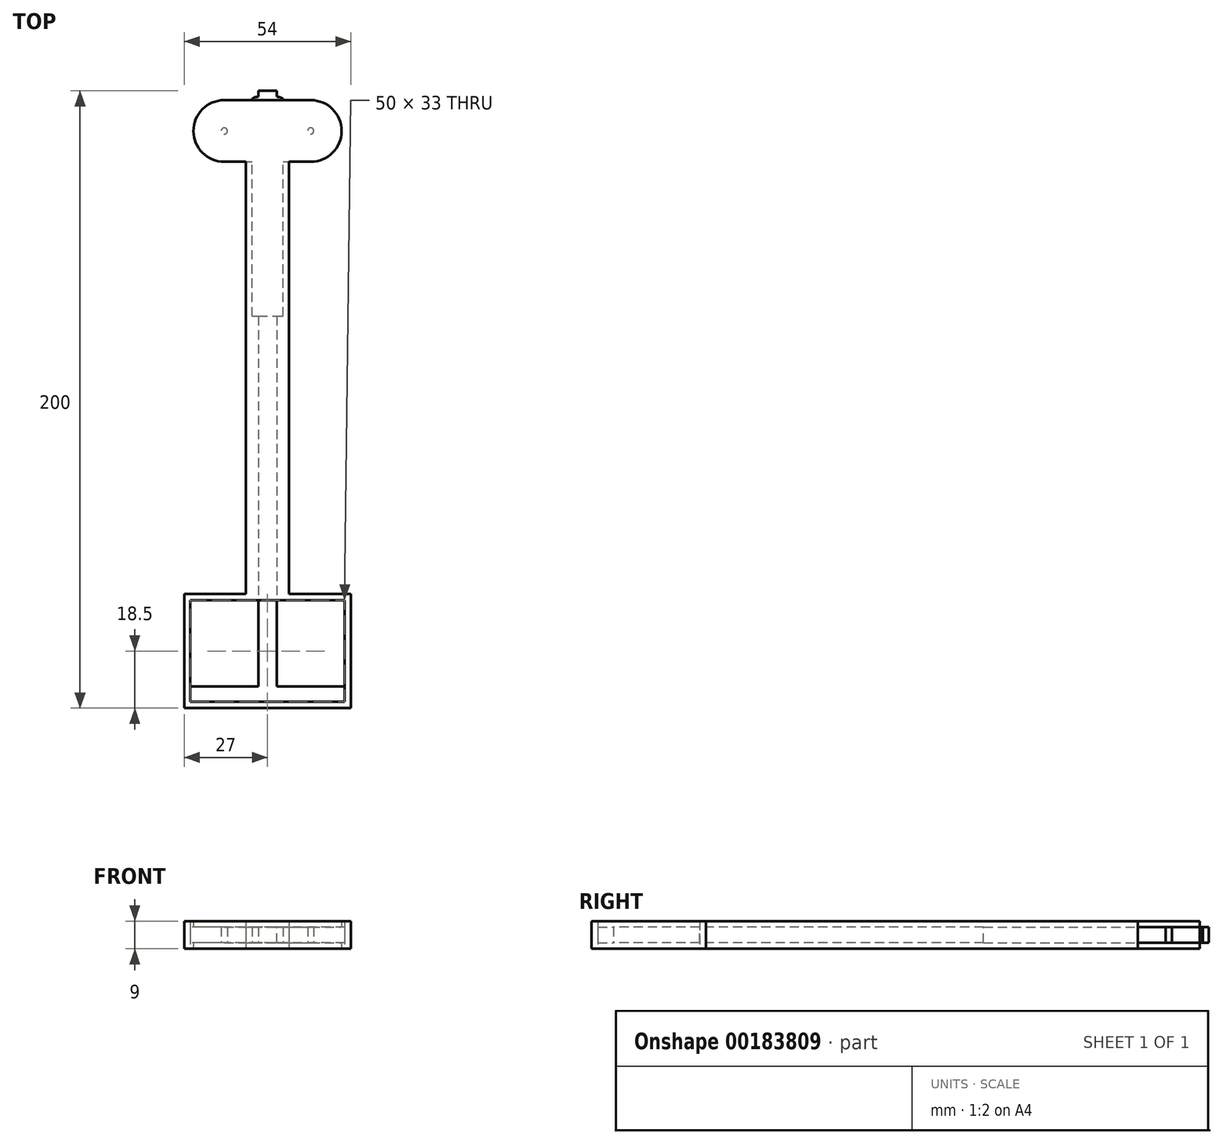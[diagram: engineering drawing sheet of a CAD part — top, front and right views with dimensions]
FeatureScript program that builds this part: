
annotation { "Feature Type Name" : "Feature", "Feature Type Description" : "" }
export const myFeature = defineFeature(function(context is Context, id is Id, definition is map)
    precondition{}
    {
        {
            var Q0;
            Q0=qCreatedBy(makeId("Top.planeOp"),FACE);
            var sketch = newSketch(context, id + "F0", { "sketchPlane" : qUnion([Q0])});
            skLineSegment(sketch, "E0.bottom", {"start": v(0, 13) * mm, "end": v(3, 13) * mm});
            skLineSegment(sketch, "E0.top", {"start": v(0, -180) * mm, "end": v(3, -180) * mm});
            skLineSegment(sketch, "E0.left", {"start": v(0, 13) * mm, "end": v(0, -180) * mm});
            skLineSegment(sketch, "E0.right", {"start": v(3, 13) * mm, "end": v(3, -180) * mm});
            skLineSegment(sketch, "E1", {"start": v(0, 10) * mm, "end": v(3, 10) * mm, "construction": true});
            skArc(sketch, "E2", {"start": v(3, 11.09) * mm, "mid": v(4.04, 10.94) * mm, "end": v(5, 10.5) * mm});
            skLineSegment(sketch, "E3", {"start": v(5, 10.5) * mm, "end": v(5, 10) * mm});
            skArc(sketch, "E4.MirrorCS", {"start": v(3, 8.91) * mm, "mid": v(4.04, 9.06) * mm, "end": v(5, 9.5) * mm});
            skLineSegment(sketch, "E5.MirrorCS", {"start": v(5, 9.5) * mm, "end": v(5, 10) * mm});
            skArc(sketch, "E6.1.0.0", {"start": v(3, 7.89) * mm, "mid": v(4.04, 7.74) * mm, "end": v(5, 7.3) * mm});
            skLineSegment(sketch, "E6.1.0.1", {"start": v(5, 7.3) * mm, "end": v(5, 6.8) * mm});
            skLineSegment(sketch, "E6.1.0.2", {"start": v(5, 6.3) * mm, "end": v(5, 6.8) * mm});
            skArc(sketch, "E6.1.0.3", {"start": v(3, 5.71) * mm, "mid": v(4.04, 5.86) * mm, "end": v(5, 6.3) * mm});
            skArc(sketch, "E6.2.0.0", {"start": v(3, 4.69) * mm, "mid": v(4.04, 4.54) * mm, "end": v(5, 4.1) * mm});
            skLineSegment(sketch, "E6.2.0.1", {"start": v(5, 4.1) * mm, "end": v(5, 3.6) * mm});
            skLineSegment(sketch, "E6.2.0.2", {"start": v(5, 3.1) * mm, "end": v(5, 3.6) * mm});
            skArc(sketch, "E6.2.0.3", {"start": v(3, 2.51) * mm, "mid": v(4.04, 2.66) * mm, "end": v(5, 3.1) * mm});
            skLineSegment(sketch, "E6.direction1", {"start": v(3, 7.39) * mm, "end": v(3, 4.19) * mm, "construction": true});
            skArc(sketch, "E7.0.3.0", {"start": v(3, 1.49) * mm, "mid": v(4.04, 1.34) * mm, "end": v(5, 0.9) * mm});
            skLineSegment(sketch, "E7.4.3.0", {"start": v(5, 0.9) * mm, "end": v(5, 0.4) * mm});
            skLineSegment(sketch, "E7.7.3.0", {"start": v(5, -0.1) * mm, "end": v(5, 0.4) * mm});
            skArc(sketch, "E7.10.3.0", {"start": v(3, -0.69) * mm, "mid": v(4.04, -0.54) * mm, "end": v(5, -0.1) * mm});
            skArc(sketch, "E7.0.4.0", {"start": v(3, -1.71) * mm, "mid": v(4.04, -1.86) * mm, "end": v(5, -2.3) * mm});
            skLineSegment(sketch, "E7.4.4.0", {"start": v(5, -2.3) * mm, "end": v(5, -2.8) * mm});
            skLineSegment(sketch, "E7.7.4.0", {"start": v(5, -3.3) * mm, "end": v(5, -2.8) * mm});
            skArc(sketch, "E7.10.4.0", {"start": v(3, -3.89) * mm, "mid": v(4.04, -3.74) * mm, "end": v(5, -3.3) * mm});
            skArc(sketch, "E7.0.5.0", {"start": v(3, -4.91) * mm, "mid": v(4.04, -5.06) * mm, "end": v(5, -5.5) * mm});
            skLineSegment(sketch, "E7.4.5.0", {"start": v(5, -5.5) * mm, "end": v(5, -6) * mm});
            skLineSegment(sketch, "E7.7.5.0", {"start": v(5, -6.5) * mm, "end": v(5, -6) * mm});
            skArc(sketch, "E7.10.5.0", {"start": v(3, -7.09) * mm, "mid": v(4.04, -6.94) * mm, "end": v(5, -6.5) * mm});
            skArc(sketch, "E7.0.6.0", {"start": v(3, -8.11) * mm, "mid": v(4.04, -8.26) * mm, "end": v(5, -8.7) * mm});
            skLineSegment(sketch, "E7.4.6.0", {"start": v(5, -8.7) * mm, "end": v(5, -9.2) * mm});
            skLineSegment(sketch, "E7.7.6.0", {"start": v(5, -9.7) * mm, "end": v(5, -9.2) * mm});
            skArc(sketch, "E7.10.6.0", {"start": v(3, -10.29) * mm, "mid": v(4.04, -10.14) * mm, "end": v(5, -9.7) * mm});
            skArc(sketch, "E7.0.7.0", {"start": v(3, -11.31) * mm, "mid": v(4.04, -11.46) * mm, "end": v(5, -11.9) * mm});
            skLineSegment(sketch, "E7.4.7.0", {"start": v(5, -11.9) * mm, "end": v(5, -12.4) * mm});
            skLineSegment(sketch, "E7.7.7.0", {"start": v(5, -12.9) * mm, "end": v(5, -12.4) * mm});
            skArc(sketch, "E7.10.7.0", {"start": v(3, -13.49) * mm, "mid": v(4.04, -13.34) * mm, "end": v(5, -12.9) * mm});
            skArc(sketch, "E7.0.8.0", {"start": v(3, -14.51) * mm, "mid": v(4.04, -14.66) * mm, "end": v(5, -15.1) * mm});
            skLineSegment(sketch, "E7.4.8.0", {"start": v(5, -15.1) * mm, "end": v(5, -15.6) * mm});
            skLineSegment(sketch, "E7.7.8.0", {"start": v(5, -16.1) * mm, "end": v(5, -15.6) * mm});
            skArc(sketch, "E7.10.8.0", {"start": v(3, -16.69) * mm, "mid": v(4.04, -16.54) * mm, "end": v(5, -16.1) * mm});
            skArc(sketch, "E7.0.9.0", {"start": v(3, -17.71) * mm, "mid": v(4.04, -17.86) * mm, "end": v(5, -18.3) * mm});
            skLineSegment(sketch, "E7.4.9.0", {"start": v(5, -18.3) * mm, "end": v(5, -18.8) * mm});
            skLineSegment(sketch, "E7.7.9.0", {"start": v(5, -19.3) * mm, "end": v(5, -18.8) * mm});
            skArc(sketch, "E7.10.9.0", {"start": v(3, -19.89) * mm, "mid": v(4.04, -19.74) * mm, "end": v(5, -19.3) * mm});
            skArc(sketch, "E7.0.10.0", {"start": v(3, -20.91) * mm, "mid": v(4.04, -21.06) * mm, "end": v(5, -21.5) * mm});
            skLineSegment(sketch, "E7.4.10.0", {"start": v(5, -21.5) * mm, "end": v(5, -22) * mm});
            skLineSegment(sketch, "E7.7.10.0", {"start": v(5, -22.5) * mm, "end": v(5, -22) * mm});
            skArc(sketch, "E7.10.10.0", {"start": v(3, -23.09) * mm, "mid": v(4.04, -22.94) * mm, "end": v(5, -22.5) * mm});
            skArc(sketch, "E7.0.11.0", {"start": v(3, -24.11) * mm, "mid": v(4.04, -24.26) * mm, "end": v(5, -24.7) * mm});
            skLineSegment(sketch, "E7.4.11.0", {"start": v(5, -24.7) * mm, "end": v(5, -25.2) * mm});
            skLineSegment(sketch, "E7.7.11.0", {"start": v(5, -25.7) * mm, "end": v(5, -25.2) * mm});
            skArc(sketch, "E7.10.11.0", {"start": v(3, -26.29) * mm, "mid": v(4.04, -26.14) * mm, "end": v(5, -25.7) * mm});
            skArc(sketch, "E7.0.12.0", {"start": v(3, -27.31) * mm, "mid": v(4.04, -27.46) * mm, "end": v(5, -27.9) * mm});
            skLineSegment(sketch, "E7.4.12.0", {"start": v(5, -27.9) * mm, "end": v(5, -28.4) * mm});
            skLineSegment(sketch, "E7.7.12.0", {"start": v(5, -28.9) * mm, "end": v(5, -28.4) * mm});
            skArc(sketch, "E7.10.12.0", {"start": v(3, -29.49) * mm, "mid": v(4.04, -29.34) * mm, "end": v(5, -28.9) * mm});
            skArc(sketch, "E7.0.13.0", {"start": v(3, -30.51) * mm, "mid": v(4.04, -30.66) * mm, "end": v(5, -31.1) * mm});
            skLineSegment(sketch, "E7.4.13.0", {"start": v(5, -31.1) * mm, "end": v(5, -31.6) * mm});
            skLineSegment(sketch, "E7.7.13.0", {"start": v(5, -32.1) * mm, "end": v(5, -31.6) * mm});
            skArc(sketch, "E7.10.13.0", {"start": v(3, -32.69) * mm, "mid": v(4.04, -32.54) * mm, "end": v(5, -32.1) * mm});
            skArc(sketch, "E7.0.14.0", {"start": v(3, -33.71) * mm, "mid": v(4.04, -33.86) * mm, "end": v(5, -34.3) * mm});
            skLineSegment(sketch, "E7.4.14.0", {"start": v(5, -34.3) * mm, "end": v(5, -34.8) * mm});
            skLineSegment(sketch, "E7.7.14.0", {"start": v(5, -35.3) * mm, "end": v(5, -34.8) * mm});
            skArc(sketch, "E7.10.14.0", {"start": v(3, -35.89) * mm, "mid": v(4.04, -35.74) * mm, "end": v(5, -35.3) * mm});
            skArc(sketch, "E7.0.15.0", {"start": v(3, -36.91) * mm, "mid": v(4.04, -37.06) * mm, "end": v(5, -37.5) * mm});
            skLineSegment(sketch, "E7.4.15.0", {"start": v(5, -37.5) * mm, "end": v(5, -38) * mm});
            skLineSegment(sketch, "E7.7.15.0", {"start": v(5, -38.5) * mm, "end": v(5, -38) * mm});
            skArc(sketch, "E7.10.15.0", {"start": v(3, -39.09) * mm, "mid": v(4.04, -38.94) * mm, "end": v(5, -38.5) * mm});
            skSolve(sketch);
        }
        {
            var Q0;
            Q0 = qSketchRegion(id + "F0", true);
            extrude(context, id + "F1", {"entities" : qUnion([Q0]), "depth" : 5 * mm});
        }
        {
            var Q0;
            Q0=makeQuery(id+"F1.opExtrude","SWEPT_BODY",BODY,{"disambiguationData":[OSD([sQuery(id+"F0.wireOp",EDGE,"E0.bottom"),sQuery(id+"F0.wireOp",EDGE,"E0.top"),sQuery(id+"F0.wireOp",EDGE,"E0.left"),sQuery(id+"F0.wireOp",EDGE,"E0.right"),sQuery(id+"F0.wireOp",EDGE,"E2"),sQuery(id+"F0.wireOp",EDGE,"E3"),sQuery(id+"F0.wireOp",EDGE,"E4.MirrorCS"),sQuery(id+"F0.wireOp",EDGE,"E5.MirrorCS"),sQuery(id+"F0.wireOp",EDGE,"E6.1.0.0"),sQuery(id+"F0.wireOp",EDGE,"E6.1.0.1"),sQuery(id+"F0.wireOp",EDGE,"E6.1.0.2"),sQuery(id+"F0.wireOp",EDGE,"E6.1.0.3"),sQuery(id+"F0.wireOp",EDGE,"E6.2.0.0"),sQuery(id+"F0.wireOp",EDGE,"E6.2.0.1"),sQuery(id+"F0.wireOp",EDGE,"E6.2.0.2"),sQuery(id+"F0.wireOp",EDGE,"E6.2.0.3"),sQuery(id+"F0.wireOp",EDGE,"E7.0.3.0"),sQuery(id+"F0.wireOp",EDGE,"E7.4.3.0"),sQuery(id+"F0.wireOp",EDGE,"E7.7.3.0"),sQuery(id+"F0.wireOp",EDGE,"E7.10.3.0"),sQuery(id+"F0.wireOp",EDGE,"E7.0.4.0"),sQuery(id+"F0.wireOp",EDGE,"E7.4.4.0"),sQuery(id+"F0.wireOp",EDGE,"E7.7.4.0"),sQuery(id+"F0.wireOp",EDGE,"E7.10.4.0"),sQuery(id+"F0.wireOp",EDGE,"E7.0.5.0"),sQuery(id+"F0.wireOp",EDGE,"E7.4.5.0"),sQuery(id+"F0.wireOp",EDGE,"E7.7.5.0"),sQuery(id+"F0.wireOp",EDGE,"E7.10.5.0"),sQuery(id+"F0.wireOp",EDGE,"E7.0.6.0"),sQuery(id+"F0.wireOp",EDGE,"E7.4.6.0"),sQuery(id+"F0.wireOp",EDGE,"E7.7.6.0"),sQuery(id+"F0.wireOp",EDGE,"E7.10.6.0"),sQuery(id+"F0.wireOp",EDGE,"E7.0.7.0"),sQuery(id+"F0.wireOp",EDGE,"E7.4.7.0"),sQuery(id+"F0.wireOp",EDGE,"E7.7.7.0"),sQuery(id+"F0.wireOp",EDGE,"E7.10.7.0"),sQuery(id+"F0.wireOp",EDGE,"E7.0.8.0"),sQuery(id+"F0.wireOp",EDGE,"E7.4.8.0"),sQuery(id+"F0.wireOp",EDGE,"E7.7.8.0"),sQuery(id+"F0.wireOp",EDGE,"E7.10.8.0"),sQuery(id+"F0.wireOp",EDGE,"E7.0.9.0"),sQuery(id+"F0.wireOp",EDGE,"E7.4.9.0"),sQuery(id+"F0.wireOp",EDGE,"E7.7.9.0"),sQuery(id+"F0.wireOp",EDGE,"E7.10.9.0"),sQuery(id+"F0.wireOp",EDGE,"E7.0.10.0"),sQuery(id+"F0.wireOp",EDGE,"E7.4.10.0"),sQuery(id+"F0.wireOp",EDGE,"E7.7.10.0"),sQuery(id+"F0.wireOp",EDGE,"E7.10.10.0"),sQuery(id+"F0.wireOp",EDGE,"E7.0.11.0"),sQuery(id+"F0.wireOp",EDGE,"E7.4.11.0"),sQuery(id+"F0.wireOp",EDGE,"E7.7.11.0"),sQuery(id+"F0.wireOp",EDGE,"E7.10.11.0"),sQuery(id+"F0.wireOp",EDGE,"E7.0.12.0"),sQuery(id+"F0.wireOp",EDGE,"E7.4.12.0"),sQuery(id+"F0.wireOp",EDGE,"E7.7.12.0"),sQuery(id+"F0.wireOp",EDGE,"E7.10.12.0"),sQuery(id+"F0.wireOp",EDGE,"E7.0.13.0"),sQuery(id+"F0.wireOp",EDGE,"E7.4.13.0"),sQuery(id+"F0.wireOp",EDGE,"E7.7.13.0"),sQuery(id+"F0.wireOp",EDGE,"E7.10.13.0"),sQuery(id+"F0.wireOp",EDGE,"E7.0.14.0"),sQuery(id+"F0.wireOp",EDGE,"E7.4.14.0"),sQuery(id+"F0.wireOp",EDGE,"E7.7.14.0"),sQuery(id+"F0.wireOp",EDGE,"E7.10.14.0"),sQuery(id+"F0.wireOp",EDGE,"E7.0.15.0"),sQuery(id+"F0.wireOp",EDGE,"E7.4.15.0"),sQuery(id+"F0.wireOp",EDGE,"E7.7.15.0"),sQuery(id+"F0.wireOp",EDGE,"E7.10.15.0")])]});
            var Q1;
            Q1=makeQuery(id+"F1.opExtrude","SWEPT_FACE",FACE,{"disambiguationData":[OSD([sQuery(id+"F0.wireOp",EDGE,"E0.left")])]});
            mirror(context, id + "F2", {"operationType" : NewBodyOperationType.ADD, "entities" : qUnion([Q0]), "mirrorPlane" : qUnion([Q1])});
        }
        {
            var Q0;
            {var subQ0=makeQuery(id+"F1.opExtrude","SWEPT_FACE",FACE,{"disambiguationData":[OSD([sQuery(id+"F0.wireOp",EDGE,"E0.top")])]});Q0=makeQuery(id+"F2.boolean.opBoolean","MERGE",FACE,{"derivedFrom":[subQ0,makeQuery(id+"F2.opPattern","COPY",FACE,{"derivedFrom":subQ0,"instanceName":"1"})]});}
            var sketch = newSketch(context, id + "F3", { "sketchPlane" : qUnion([Q0])});
            skLineSegment(sketch, "E8.bottom", {"start": v(25, 5) * mm, "end": v(-25, 5) * mm});
            skLineSegment(sketch, "E8.top", {"start": v(25, 0) * mm, "end": v(-25, 0) * mm});
            skLineSegment(sketch, "E8.left", {"start": v(25, 5) * mm, "end": v(25, 0) * mm});
            skLineSegment(sketch, "E8.right", {"start": v(-25, 5) * mm, "end": v(-25, 0) * mm});
            skPoint(sketch, "E8.middle", {"position": v(0, 2.5) * mm});
            skPoint(sketch, "E8.middle.positionSnap0", {"position": v(-3, 2.5) * mm});
            skPoint(sketch, "E8.centerSnap0", {"position": v(-3, 2.5) * mm});
            skSolve(sketch);
        }
        {
            var Q0;
            Q0 = qSketchRegion(id + "F3", true);
            extrude(context, id + "F4", {"entities" : qUnion([Q0]), "operationType" : NewBodyOperationType.ADD, "depth" : 5 * mm});
        }
        {
            var Q0;
            Q0=qCreatedBy(makeId("Top.planeOp"),FACE);
            var sketch = newSketch(context, id + "F5", { "sketchPlane" : qUnion([Q0])});
            skCircle(sketch, "E9", {"center": v(14, 0) * mm, "radius": 10 * mm});
            skLineSegment(sketch, "E10", {"start": v(0, 10) * mm, "end": v(14, 10) * mm});
            skLineSegment(sketch, "E11", {"start": v(0, -187) * mm, "end": v(27, -187) * mm});
            skLineSegment(sketch, "E12", {"start": v(27, -187) * mm, "end": v(27, -150) * mm});
            skLineSegment(sketch, "E13", {"start": v(27, -150) * mm, "end": v(7, -150) * mm});
            skLineSegment(sketch, "E14", {"start": v(7, -150) * mm, "end": v(7, -10) * mm});
            skLineSegment(sketch, "E15", {"start": v(7, -10) * mm, "end": v(14, -10) * mm});
            skLineSegment(sketch, "E16.MirrorCS", {"start": v(0, 10) * mm, "end": v(-14, 10) * mm});
            skCircle(sketch, "E17.MirrorC", {"center": v(-14, 0) * mm, "radius": 10 * mm});
            skLineSegment(sketch, "E18.MirrorCS", {"start": v(-7, -10) * mm, "end": v(-14, -10) * mm});
            skLineSegment(sketch, "E19.MirrorCS", {"start": v(-7, -150) * mm, "end": v(-7, -10) * mm});
            skLineSegment(sketch, "E20.MirrorCS", {"start": v(-27, -150) * mm, "end": v(-7, -150) * mm});
            skLineSegment(sketch, "E21.MirrorCS", {"start": v(-27, -187) * mm, "end": v(-27, -150) * mm});
            skLineSegment(sketch, "E22.MirrorCS", {"start": v(0, -187) * mm, "end": v(-27, -187) * mm});
            skLineSegment(sketch, "E23.bottom", {"start": v(25, -152) * mm, "end": v(-25, -152) * mm});
            skLineSegment(sketch, "E23.top", {"start": v(25, -185) * mm, "end": v(-25, -185) * mm});
            skLineSegment(sketch, "E23.left", {"start": v(25, -152) * mm, "end": v(25, -185) * mm});
            skLineSegment(sketch, "E23.right", {"start": v(-25, -152) * mm, "end": v(-25, -185) * mm});
            skPoint(sketch, "E23.middle", {"position": v(0, -168.5) * mm});
            skSolve(sketch);
        }
        {
            var Q0;
            Q0 = qSketchRegion(id + "F5", true);
            extrude(context, id + "F6", {"entities" : qUnion([Q0]), "depth" : 7 * mm, "hasSecondDirection" : true, "secondDirectionOppositeDirection" : true, "secondDirectionDepth" : 2 * mm});
        }
        {
            var Q0;
            Q0=makeQuery(id+"F1.opExtrude","SWEPT_BODY",BODY,{"disambiguationData":[OSD([sQuery(id+"F0.wireOp",EDGE,"E0.bottom"),sQuery(id+"F0.wireOp",EDGE,"E0.top"),sQuery(id+"F0.wireOp",EDGE,"E0.left"),sQuery(id+"F0.wireOp",EDGE,"E0.right"),sQuery(id+"F0.wireOp",EDGE,"E2"),sQuery(id+"F0.wireOp",EDGE,"E3"),sQuery(id+"F0.wireOp",EDGE,"E4.MirrorCS"),sQuery(id+"F0.wireOp",EDGE,"E5.MirrorCS"),sQuery(id+"F0.wireOp",EDGE,"E6.1.0.0"),sQuery(id+"F0.wireOp",EDGE,"E6.1.0.1"),sQuery(id+"F0.wireOp",EDGE,"E6.1.0.2"),sQuery(id+"F0.wireOp",EDGE,"E6.1.0.3"),sQuery(id+"F0.wireOp",EDGE,"E6.2.0.0"),sQuery(id+"F0.wireOp",EDGE,"E6.2.0.1"),sQuery(id+"F0.wireOp",EDGE,"E6.2.0.2"),sQuery(id+"F0.wireOp",EDGE,"E6.2.0.3"),sQuery(id+"F0.wireOp",EDGE,"E7.0.3.0"),sQuery(id+"F0.wireOp",EDGE,"E7.4.3.0"),sQuery(id+"F0.wireOp",EDGE,"E7.7.3.0"),sQuery(id+"F0.wireOp",EDGE,"E7.10.3.0"),sQuery(id+"F0.wireOp",EDGE,"E7.0.4.0"),sQuery(id+"F0.wireOp",EDGE,"E7.4.4.0"),sQuery(id+"F0.wireOp",EDGE,"E7.7.4.0"),sQuery(id+"F0.wireOp",EDGE,"E7.10.4.0"),sQuery(id+"F0.wireOp",EDGE,"E7.0.5.0"),sQuery(id+"F0.wireOp",EDGE,"E7.4.5.0"),sQuery(id+"F0.wireOp",EDGE,"E7.7.5.0"),sQuery(id+"F0.wireOp",EDGE,"E7.10.5.0"),sQuery(id+"F0.wireOp",EDGE,"E7.0.6.0"),sQuery(id+"F0.wireOp",EDGE,"E7.4.6.0"),sQuery(id+"F0.wireOp",EDGE,"E7.7.6.0"),sQuery(id+"F0.wireOp",EDGE,"E7.10.6.0"),sQuery(id+"F0.wireOp",EDGE,"E7.0.7.0"),sQuery(id+"F0.wireOp",EDGE,"E7.4.7.0"),sQuery(id+"F0.wireOp",EDGE,"E7.7.7.0"),sQuery(id+"F0.wireOp",EDGE,"E7.10.7.0"),sQuery(id+"F0.wireOp",EDGE,"E7.0.8.0"),sQuery(id+"F0.wireOp",EDGE,"E7.4.8.0"),sQuery(id+"F0.wireOp",EDGE,"E7.7.8.0"),sQuery(id+"F0.wireOp",EDGE,"E7.10.8.0"),sQuery(id+"F0.wireOp",EDGE,"E7.0.9.0"),sQuery(id+"F0.wireOp",EDGE,"E7.4.9.0"),sQuery(id+"F0.wireOp",EDGE,"E7.7.9.0"),sQuery(id+"F0.wireOp",EDGE,"E7.10.9.0"),sQuery(id+"F0.wireOp",EDGE,"E7.0.10.0"),sQuery(id+"F0.wireOp",EDGE,"E7.4.10.0"),sQuery(id+"F0.wireOp",EDGE,"E7.7.10.0"),sQuery(id+"F0.wireOp",EDGE,"E7.10.10.0"),sQuery(id+"F0.wireOp",EDGE,"E7.0.11.0"),sQuery(id+"F0.wireOp",EDGE,"E7.4.11.0"),sQuery(id+"F0.wireOp",EDGE,"E7.7.11.0"),sQuery(id+"F0.wireOp",EDGE,"E7.10.11.0"),sQuery(id+"F0.wireOp",EDGE,"E7.0.12.0"),sQuery(id+"F0.wireOp",EDGE,"E7.4.12.0"),sQuery(id+"F0.wireOp",EDGE,"E7.7.12.0"),sQuery(id+"F0.wireOp",EDGE,"E7.10.12.0"),sQuery(id+"F0.wireOp",EDGE,"E7.0.13.0"),sQuery(id+"F0.wireOp",EDGE,"E7.4.13.0"),sQuery(id+"F0.wireOp",EDGE,"E7.7.13.0"),sQuery(id+"F0.wireOp",EDGE,"E7.10.13.0"),sQuery(id+"F0.wireOp",EDGE,"E7.0.14.0"),sQuery(id+"F0.wireOp",EDGE,"E7.4.14.0"),sQuery(id+"F0.wireOp",EDGE,"E7.7.14.0"),sQuery(id+"F0.wireOp",EDGE,"E7.10.14.0"),sQuery(id+"F0.wireOp",EDGE,"E7.0.15.0"),sQuery(id+"F0.wireOp",EDGE,"E7.4.15.0"),sQuery(id+"F0.wireOp",EDGE,"E7.7.15.0"),sQuery(id+"F0.wireOp",EDGE,"E7.10.15.0")])]});
            var Q1;
            Q1=makeQuery(id+"F6.opExtrude","SWEPT_BODY",BODY,{"disambiguationData":[OSD([sQuery(id+"F5.wireOp",EDGE,"E9"),sQuery(id+"F5.wireOp",EDGE,"E10"),sQuery(id+"F5.wireOp",EDGE,"E11"),sQuery(id+"F5.wireOp",EDGE,"E12"),sQuery(id+"F5.wireOp",EDGE,"E13"),sQuery(id+"F5.wireOp",EDGE,"E14"),sQuery(id+"F5.wireOp",EDGE,"E15"),sQuery(id+"F5.wireOp",EDGE,"E16.MirrorCS"),sQuery(id+"F5.wireOp",EDGE,"E17.MirrorC"),sQuery(id+"F5.wireOp",EDGE,"E18.MirrorCS"),sQuery(id+"F5.wireOp",EDGE,"E19.MirrorCS"),sQuery(id+"F5.wireOp",EDGE,"E20.MirrorCS"),sQuery(id+"F5.wireOp",EDGE,"E21.MirrorCS"),sQuery(id+"F5.wireOp",EDGE,"E22.MirrorCS"),sQuery(id+"F5.wireOp",EDGE,"E23.bottom"),sQuery(id+"F5.wireOp",EDGE,"E23.top"),sQuery(id+"F5.wireOp",EDGE,"E23.left"),sQuery(id+"F5.wireOp",EDGE,"E23.right")])]});
            booleanBodies(context, id + "F7", {"operationType" : BooleanOperationType.SUBTRACTION, "tools" : qUnion([Q0]), "targets" : qUnion([Q1]), "keepTools" : true});
        }
        {
            var Q0;
            Q0=qCreatedBy(makeId("Top.planeOp"),FACE);
            var sketch = newSketch(context, id + "F8", { "sketchPlane" : qUnion([Q0])});
            skArc(sketch, "E24.0", {"start": v(-14, -10) * mm, "mid": v(-24, 0) * mm, "end": v(-14, 10) * mm});
            skLineSegment(sketch, "E25.0", {"start": v(-14, 10) * mm, "end": v(14, 10) * mm});
            skArc(sketch, "E26.0", {"start": v(14, -10) * mm, "mid": v(24, 0) * mm, "end": v(14, 10) * mm});
            skLineSegment(sketch, "E27", {"start": v(-14, -10) * mm, "end": v(14, -10) * mm});
            skSolve(sketch);
        }
        {
            var Q0;
            Q0 = qSketchRegion(id + "F8", true);
            extrude(context, id + "F9", {"entities" : qUnion([Q0]), "operationType" : NewBodyOperationType.REMOVE, "depth" : 5 * mm});
        }
        {
            var Q0;
            {var subQ69=sQuery(id+"F8.wireOp",EDGE,"E27");Q0=makeQuery(id+"F9.boolean.opBoolean","COPY",FACE,{"disambiguationData":[TD([makeQuery(id+"F6.opExtrude","SWEPT_FACE",FACE,{"disambiguationData":[OSD([sQuery(id+"F5.wireOp",EDGE,"E18.MirrorCS")])]})])],"derivedFrom":makeQuery(id+"F9.opExtrude","SWEPT_FACE",FACE,{"disambiguationData":[OSD([subQ69])]})});}
            var sketch = newSketch(context, id + "F10", { "sketchPlane" : qUnion([Q0])});
            skLineSegment(sketch, "E28.bottom", {"start": v(5, 5) * mm, "end": v(-5, 5) * mm});
            skLineSegment(sketch, "E28.top", {"start": v(5, 0) * mm, "end": v(-5, 0) * mm});
            skLineSegment(sketch, "E28.left", {"start": v(5, 5) * mm, "end": v(5, 0) * mm});
            skLineSegment(sketch, "E28.right", {"start": v(-5, 5) * mm, "end": v(-5, 0) * mm});
            skSolve(sketch);
        }
        {
            var Q0;
            Q0 = qSketchRegion(id + "F10", true);
            extrude(context, id + "F11", {"entities" : qUnion([Q0]), "operationType" : NewBodyOperationType.REMOVE, "oppositeDirection" : true, "depth" : 50 * mm});
        }
        {
            var Q0;
            Q0=qCreatedBy(makeId("Top.planeOp"),FACE);
            var sketch = newSketch(context, id + "F12", { "sketchPlane" : qUnion([Q0])});
            skCircle(sketch, "E29", {"center": v(14, 0) * mm, "radius": 1 * mm});
            skCircle(sketch, "E30", {"center": v(-14, 0) * mm, "radius": 1 * mm});
            skSolve(sketch);
        }
        {
            var Q0;
            Q0 = qSketchRegion(id + "F12", true);
            extrude(context, id + "F13", {"entities" : qUnion([Q0]), "operationType" : NewBodyOperationType.ADD, "endBound" : BoundingType.UP_TO_NEXT, "depth" : 25 * mm});
        }
    });
